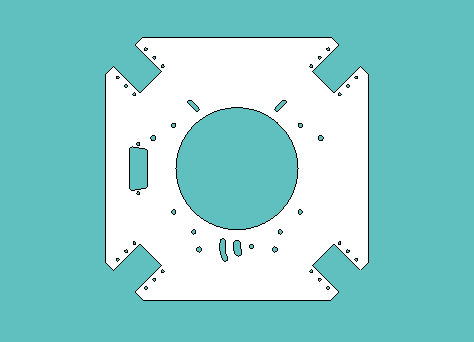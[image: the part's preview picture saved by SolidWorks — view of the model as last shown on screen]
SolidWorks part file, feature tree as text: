
SOLIDWORKS PART (.sldprt)
format: sldprt  version: not decoded by parser v0  size: 1,054,208 bytes
history: native  units: mm
features: sketch x7, cut_extrude x5, plane x2, material x1, extrude x1, fillet x1 (+11 scaffold rows collapsed)
feature tree (28):
  scaffold x11  (default folders/planes/origin — collapsed)
  material  "Material <not specified>"
  sketch  "Sketch1"  dims[c1.D1=57.15mm c1.D11=1.9812mm c1.D12=1.9812mm c1.D13=1.9812mm c1.D18=19.05mm c1.D21=2.9464mm c1.D24=3.2639mm c1.D25=3.2639mm c1.D26=3.2639mm c1.D27=3.2639mm c1.D28=~2.77622mm c1.D29=~2.77622mm c1.D30=~2.77622mm c1.D31=~2.77622mm c1.D32=3.2639mm c1.D33=3.2639mm c1.D34=3.2639mm c1.D17=~3.96875mm c2.D18=~3.96875mm c2.D19=~3.96875mm c2.D20=3.4544mm c2.D21=3.4544mm c2.D22=34.29mm c2.D24=19.05mm c2.D25=19.05mm c2.D26=82.55mm c3.D18=9.525mm c3.D1=~81.605366mm c4.D1=45.0deg c4.D2=~75.797233mm c5.D2=45.0deg c5.D3=82.55mm c5.D4=88.9mm c5.D5=88.9mm c5.D6=82.55mm c6.D2=63.5mm c6.D3=20.32mm c6.D6=10.16mm c6.D7=25.4mm c6.D8=63.5mm c6.D9=26.9748mm c6.D10=13.4874mm c6.D14=7.1374mm c6.D15=8.001mm c6.D16=8.001mm c7.D14=7.1374mm c7.D17=153.9748mm c7.D19=~96.70302mm c8.D19=15.0deg c8.D20=~95.476034mm c9.D20=15.0deg c9.D22=114.3mm c9.D23=~205.470614mm c10.D23=90.0deg c10.D24=9.525mm c10.D25=9.525mm c10.D17=6.5mm c10.D19=~75.74929mm c10.D20=~75.74929mm]
  extrude  "Extrude1"  Depth=3.175mm
  plane  "Plane1"
  plane  "Plane2"
  sketch  "Sketch3"  dims[D1=90.551mm D2=9.0678mm D3=99.6188mm]
  sketch  "Sketch2"  dims[c1.D3=4.7625mm c1.D4=2.159mm c1.D5=2.159mm c1.D6=105.156mm c1.D7=3.4544mm c1.D9=~3.571875mm c1.D2=~3.571875mm c2.D4=~2.778125mm c2.D1=~89.220661mm c3.D1=120.0deg c3.D2=~89.220661mm c4.D2=120.0deg c4.D8=6.985mm c4.D10=~9.92124mm c4.D11=~9.92124mm c4.D12=~2.38125mm c4.D5=~30.045999mm c5.D5=10.0deg c5.D7=~30.045999mm c6.D7=25.0deg c6.D9=52.578mm]
  cut_extrude  "Cut-Extrude1"  [1 undecoded]
  sketch  "Sketch7"  dims[c1.D3=13.0302mm c1.D4=13.0302mm c1.D5=13.0302mm c1.D6=~5.55625mm c1.D7=~5.55625mm c1.D8=~5.55625mm c1.D9=88.9mm c1.D10=101.6mm c1.D2=88.9mm c1.D11=2.9464mm c1.D12=2.9464mm c1.D14=2.9464mm c1.D15=2.9464mm c1.D17=2.9464mm c1.D18=2.9464mm c1.D19=2.9464mm c1.D23=19.05mm c1.D24=19.05mm c2.D23=9.525mm c2.D1=~90.36024mm c3.D1=135.0deg c3.D2=~90.36024mm c4.D2=135.0deg c5.D2=~90.36024mm c6.D2=135.0deg c6.D9=~90.36024mm c7.D9=90.0deg c7.D10=19.05mm c7.D13=19.05mm c7.D16=19.05mm c7.D19=~2.38125mm c7.D12=~92.589635mm c8.D12=45.0deg c8.D20=~91.404222mm c9.D20=45.0deg c9.D21=19.05mm c10.D21=20.0deg c10.D22=19.05mm c11.D22=20.0deg c11.D23=9.525mm c11.D21=19.05mm c12.D21=10.0deg c12.D22=19.05mm c13.D22=10.0deg]
  cut_extrude  "Cut-Extrude3"  [1 undecoded]
  sketch  "Sketch8"  dims[c1.D1=114.3mm c1.D3=3.4544mm c1.D4=3.4544mm c1.D5=3.4544mm c1.D6=3.4544mm c2.D5=120.65mm c2.D8=3.4544mm c2.D2=~203.517429mm c3.D2=25.0deg c3.D4=~193.161651mm c4.D4=110.0deg c4.D7=~138.918946mm c5.D7=25.0deg]
  cut_extrude  "Cut-Extrude4"  [1 undecoded]
  sketch  "Sketch10"  dims[D1=2.159mm D2=2.159mm]
  cut_extrude  "Cut-Extrude5"  [1 undecoded]
  sketch  "Sketch11"  dims[D1=~0.79375mm D2=~0.79375mm D3=~0.79375mm D4=~0.79375mm]
  cut_extrude  "Cut-Extrude6"  [1 undecoded]
  fillet  "Fillet1"  Radius=2.38125mm
decode coverage: 9 of 14 modeling features carry decoded parameters
note: ~ marks probable driven/reference dimensions
note: 5 parameter values undecoded
summary: no parameter record found for 5 features
note: suppression state not decoded; provenance and decode notes live in map.json
